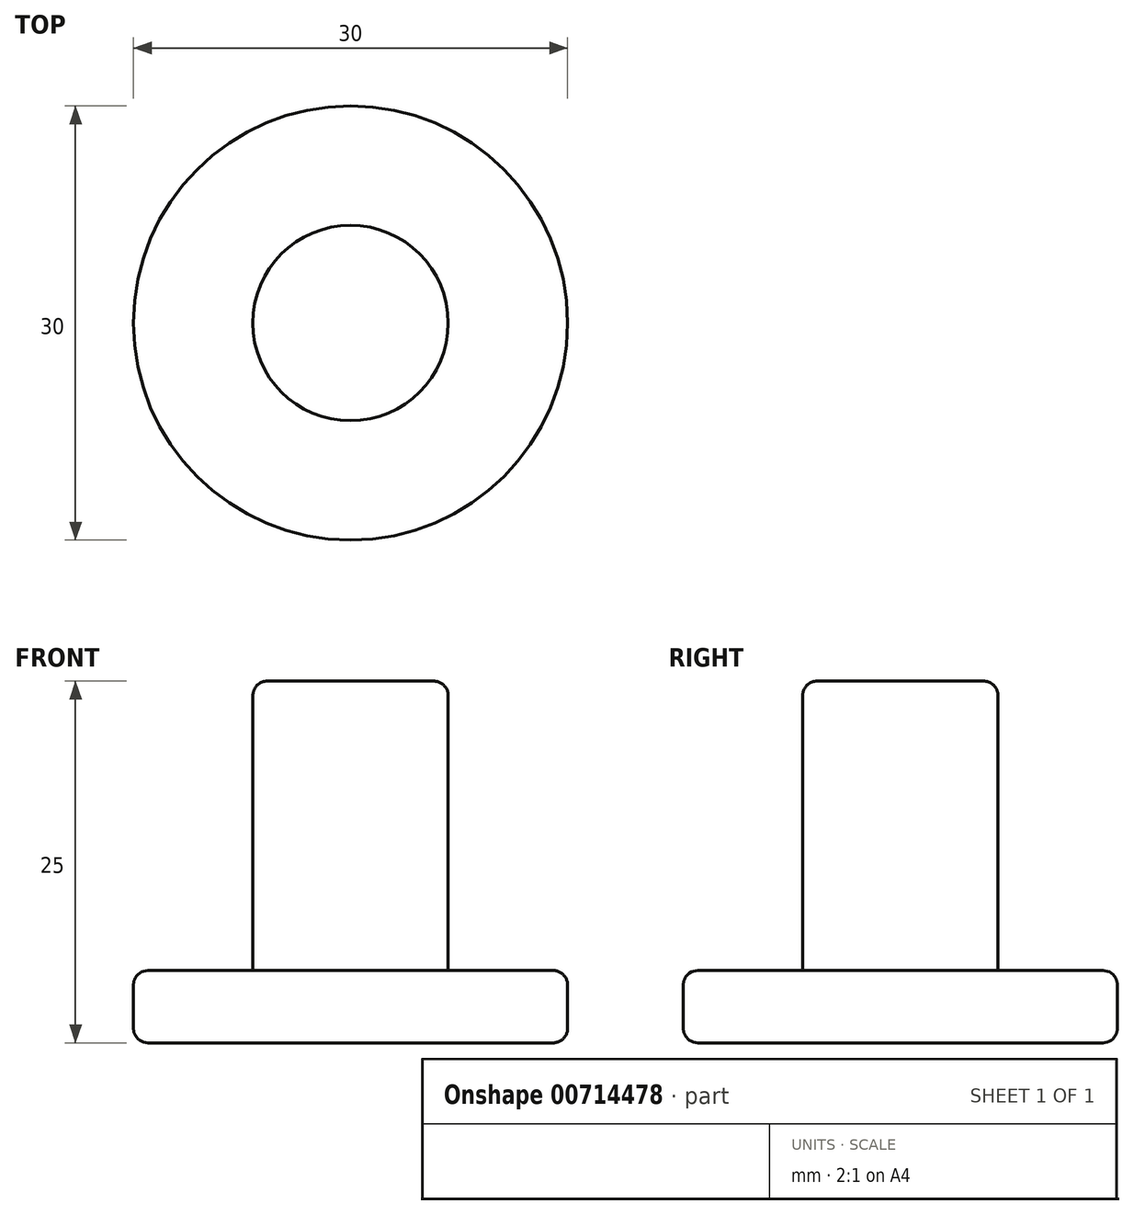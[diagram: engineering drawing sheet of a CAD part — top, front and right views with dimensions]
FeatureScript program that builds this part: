
annotation { "Feature Type Name" : "Feature", "Feature Type Description" : "" }
export const myFeature = defineFeature(function(context is Context, id is Id, definition is map)
    precondition{}
    {
        {
            var Q0;
            Q0=qCreatedBy(makeId("Top.planeOp"),FACE);
            var sketch = newSketch(context, id + "F0", { "sketchPlane" : qUnion([Q0])});
            skCircle(sketch, "E0", {"center": v(0, 0) * mm, "radius": 15 * mm});
            skCircle(sketch, "E1", {"center": v(0, 0) * mm, "radius": 6.75 * mm});
            skSolve(sketch);
        }
        {
            var Q0;
            Q0=makeQuery(id+"F0.imprint","IMPRINT",FACE,{"disambiguationData":[TD([[makeQuery(id+"F0.imprint","IMPRINT",EDGE,{"derivedFrom":sQuery(id+"F0.wireOp",EDGE,"E1")}),1.0]])]});
            extrude(context, id + "F1", {"entities" : qUnion([Q0]), "depth" : 25 * mm, "offsetDistance" : 25 * mm});
        }
        {
            var Q0;
            Q0=makeQuery(id+"F0.imprint","IMPRINT",FACE,{"disambiguationData":[TD([[makeQuery(id+"F0.imprint","IMPRINT",EDGE,{"derivedFrom":sQuery(id+"F0.wireOp",EDGE,"E0")}),1.0]])]});
            extrude(context, id + "F2", {"entities" : qUnion([Q0]), "operationType" : NewBodyOperationType.ADD, "depth" : 5 * mm, "offsetDistance" : 25 * mm});
        }
        {
            var Q0;
            Q0=makeQuery(id+"F2.opExtrude","CAP_EDGE",EDGE,{"disambiguationData":[OSD([sQuery(id+"F0.wireOp",EDGE,"E0")])],"isStart":true});
            var Q1;
            Q1=makeQuery(id+"F2.opExtrude","CAP_EDGE",EDGE,{"disambiguationData":[OSD([sQuery(id+"F0.wireOp",EDGE,"E0")])],"isStart":false});
            var Q2;
            Q2=makeQuery(id+"F1.opExtrude","CAP_FACE",FACE,{"disambiguationData":[OSD([sQuery(id+"F0.wireOp",EDGE,"E1")])],"isStart":false});
            fillet(context, id + "F3", {"entities" : qUnion([Q0, Q1, Q2]), "radius" : 1 * mm, "tangentPropagation" : true, "allowEdgeOverflow" : false});
        }
    });
